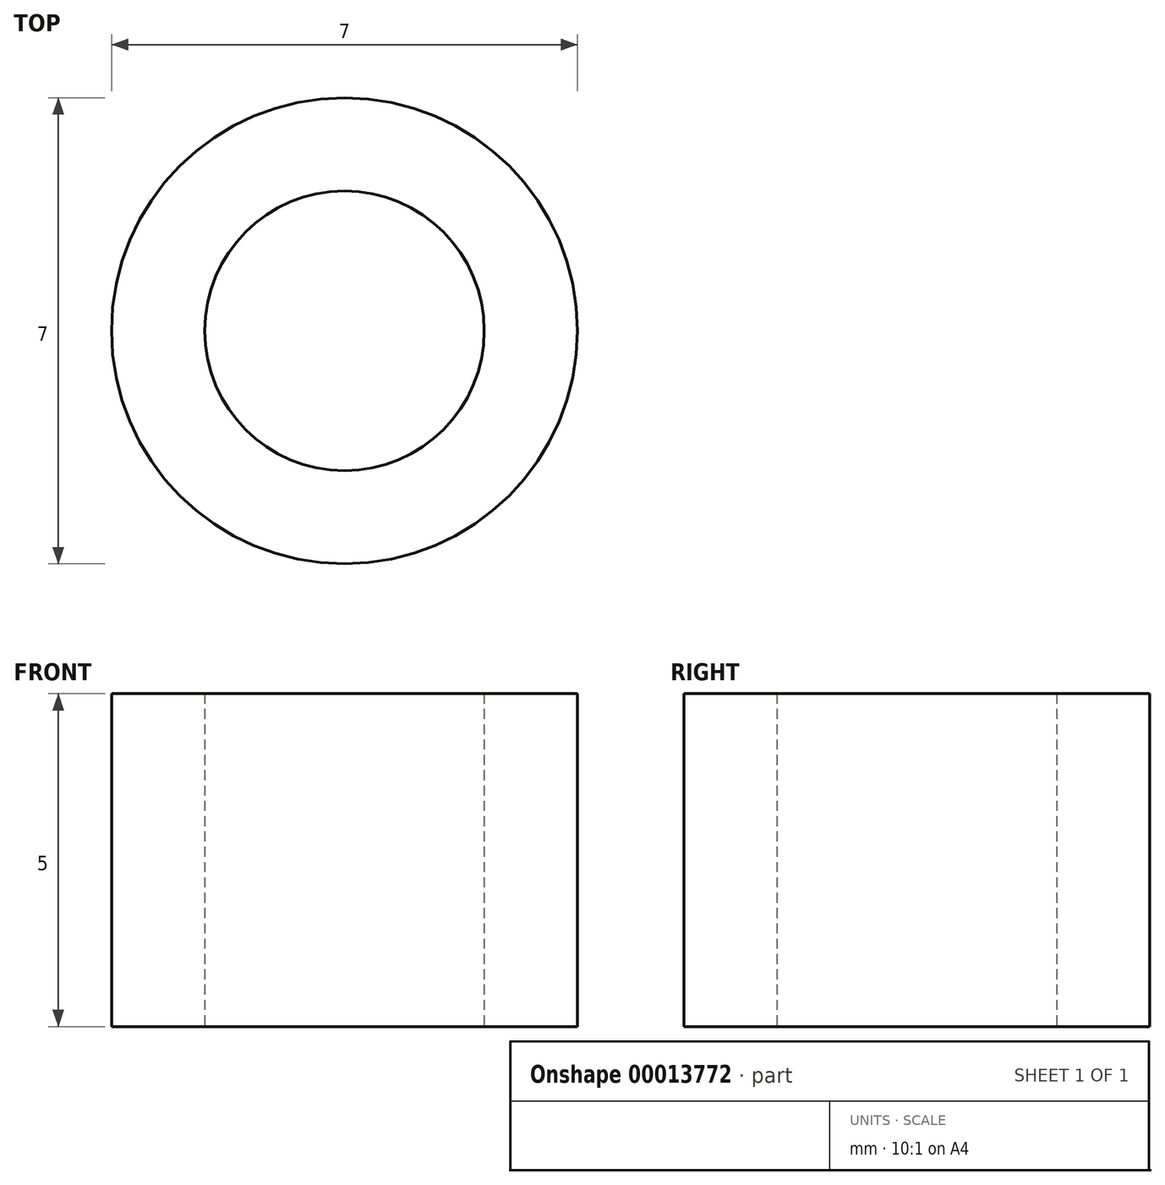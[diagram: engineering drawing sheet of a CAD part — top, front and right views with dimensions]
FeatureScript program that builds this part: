
annotation { "Feature Type Name" : "Feature", "Feature Type Description" : "" }
export const myFeature = defineFeature(function(context is Context, id is Id, definition is map)
    precondition{}
    {
        {
            var Q0;
            Q0=qCreatedBy(makeId("Top.planeOp"),FACE);
            var sketch = newSketch(context, id + "F0", { "sketchPlane" : qUnion([Q0])});
            skCircle(sketch, "E0", {"center": v(0, 0) * mm, "radius": 2.1 * mm});
            skCircle(sketch, "E1", {"center": v(0, 0) * mm, "radius": 3.5 * mm});
            skSolve(sketch);
        }
        {
            var Q0;
            Q0=makeQuery(id+"F0.imprint","IMPRINT",FACE,{"disambiguationData":[TD([[makeQuery(id+"F0.imprint","IMPRINT",EDGE,{"derivedFrom":sQuery(id+"F0.wireOp",EDGE,"E0")}),-1.0]])]});
            extrude(context, id + "F1", {"entities" : qUnion([Q0]), "depth" : 5 * mm});
        }
    });
